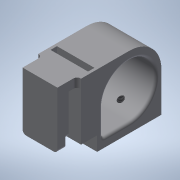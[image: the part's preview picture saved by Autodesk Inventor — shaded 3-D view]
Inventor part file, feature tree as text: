
AUTODESK INVENTOR PART (.ipt)
format: ipt  version: 2022 (Build 260153000, 153)  size: 247,296 bytes
history: native  units: mm
features: fillet x8, extrude x5, sketch x5, hole x1, chamfer x1
ambient origin geometry x8: Origin, YZ Plane, XZ Plane, XY Plane, X Axis, Y Axis, Z Axis, Center Point
bodies: Volumenkörper1 (feature_tree)
feature tree (20):
  extrude  "Extrusion1"  Depth=24.0mm
  extrude  "Extrusion2"  Depth=3.0mm
  fillet  "Rundung1"  Radius=26.0mm
  fillet  "Rundung2"  Radius=15.0mm
  fillet  "Rundung3"  Radius=15.0mm
  extrude  "Extrusion4"  Depth=15.0mm
  hole  "Bohrung2"  [1 undecoded]
  fillet  "Rundung10"  Radius=36.0mm
  fillet  "Rundung12"  Radius=40.0mm
  chamfer  "Fase1"  Distance=32.0mm
  extrude  "Extrusion5"  Depth=5.0mm
  extrude  "Extrusion6"  Depth=21.0mm
  fillet  "Rundung16"  Radius=3.6mm
  fillet  "Rundung14"  Radius=8.0mm
  fillet  "Rundung15"  Radius=10.8mm
  sketch  "Skizze2"  dims[d2=24.0mm d3=0.0mm d4=30.0mm]
  sketch  "Skizze5"  dims[d5=30.0mm d6=3.0mm d8=26.0mm d9=0.0mm d10=15.0mm d11=15.0mm]
  sketch  "Skizze6"  dims[d12=18.0mm d36=15.0mm]
  sketch  "Skizze7"  dims[d38=1.5mm d40=0.5mm d41=2.0mm d42=45.0deg d43=36.0mm d45=40.0mm]
  sketch  "Skizze8"  dims[d46=45.0mm d47=32.0mm d49=5.0mm d50=21.0mm d51=3.6mm d52=8.0mm d53=0.0mm d55=10.8mm d56=3.242mm d57=8.0mm d58=4.0mm d59=2.0mm d60=90.0deg d61=11.8mm d62=20.594885mm d66=6.5mm d67=0.0mm d68=4.5mm d69=0.0mm d70=10.0mm d71=1.5mm d73=19.5mm d74=5.0mm d75=10.0mm d77=2.0mm d72=0.5mm]
note: 1 required parameter value undecoded (feature->parameter linkage not recoverable at this tier; creation-order binding heuristic only, values carry confidence <= 0.55)
